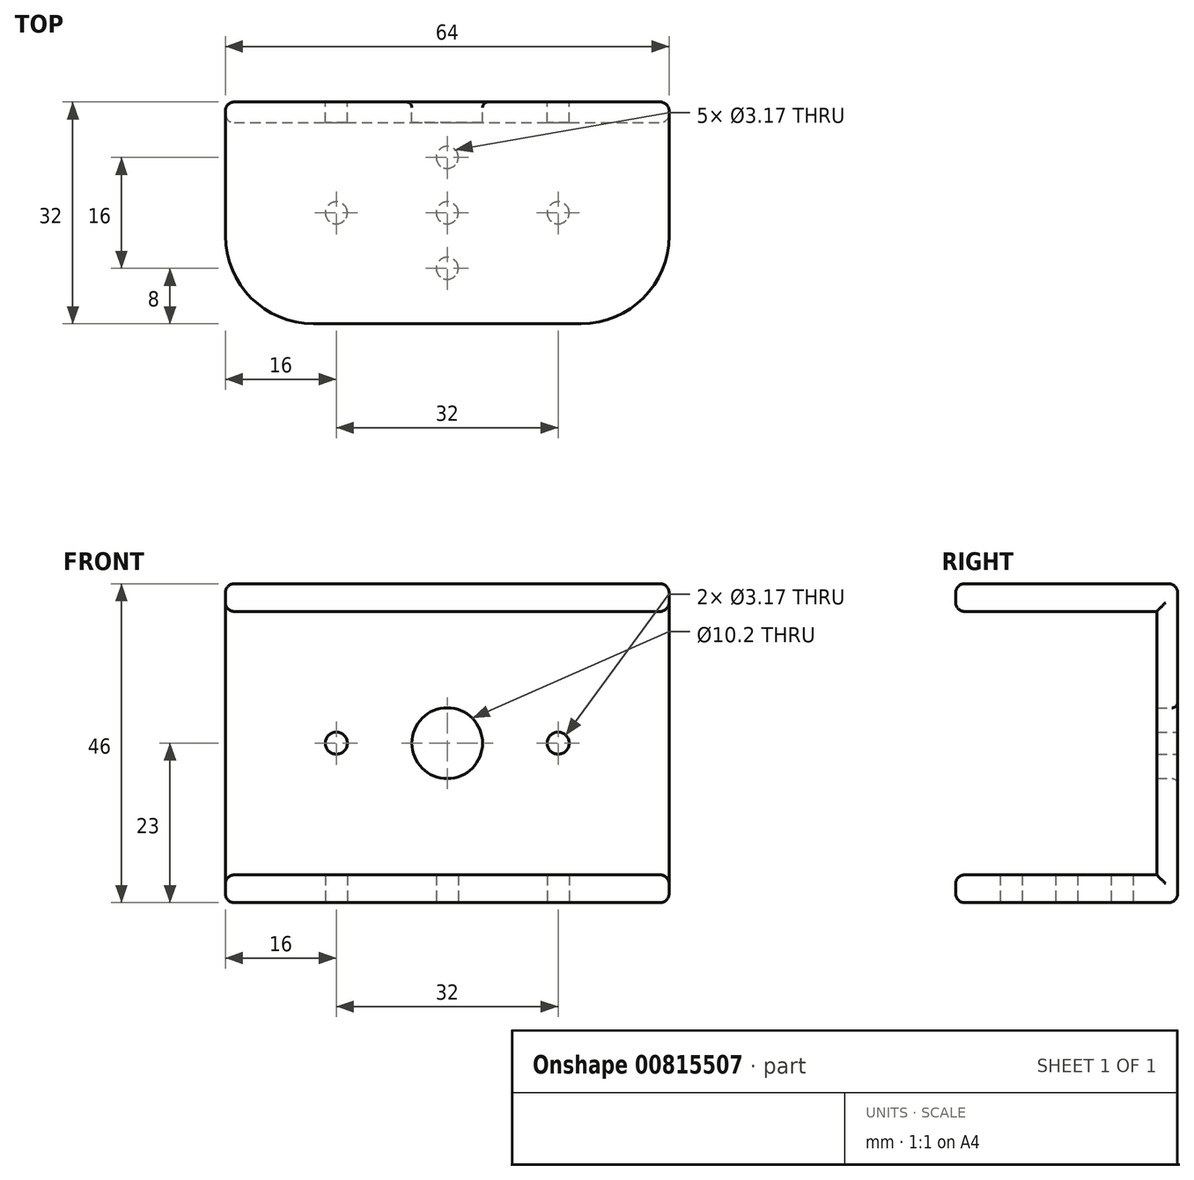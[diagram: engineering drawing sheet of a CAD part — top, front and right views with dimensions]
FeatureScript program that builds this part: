
annotation { "Feature Type Name" : "Feature", "Feature Type Description" : "" }
export const myFeature = defineFeature(function(context is Context, id is Id, definition is map)
    precondition{}
    {
        {
            var Q0;
            Q0=qCreatedBy(makeId("Front.planeOp"),FACE);
            var sketch = newSketch(context, id + "F0", { "sketchPlane" : qUnion([Q0])});
            skLineSegment(sketch, "E0", {"start": v(64, 0) * mm, "end": v(64, 38) * mm});
            skLineSegment(sketch, "E1", {"start": v(64, 38) * mm, "end": v(0, 38) * mm});
            skLineSegment(sketch, "E2", {"start": v(0, 38) * mm, "end": v(0, 0) * mm});
            skLineSegment(sketch, "E3", {"start": v(0, 0) * mm, "end": v(64, 0) * mm});
            skLineSegment(sketch, "E4", {"start": v(0, 19) * mm, "end": v(64, 19) * mm, "construction": true});
            skLineSegment(sketch, "E5", {"start": v(32, 38) * mm, "end": v(32, 0) * mm, "construction": true});
            skCircle(sketch, "E6", {"center": v(32, 19) * mm, "radius": 5.1 * mm});
            skLineSegment(sketch, "E7", {"start": v(0, 19) * mm, "end": v(32, 19) * mm, "construction": true});
            skLineSegment(sketch, "E8", {"start": v(32, 19) * mm, "end": v(64, 19) * mm, "construction": true});
            skCircle(sketch, "E9", {"center": v(16, 19) * mm, "radius": 1.59 * mm});
            skCircle(sketch, "E10", {"center": v(48, 19) * mm, "radius": 1.59 * mm});
            skLineSegment(sketch, "E11", {"start": v(0, 38) * mm, "end": v(0, 42) * mm});
            skLineSegment(sketch, "E12", {"start": v(0, 42) * mm, "end": v(64, 42) * mm});
            skLineSegment(sketch, "E13", {"start": v(64, 42) * mm, "end": v(64, 38) * mm});
            skLineSegment(sketch, "E14", {"start": v(64, 0) * mm, "end": v(64, -4) * mm});
            skLineSegment(sketch, "E15", {"start": v(64, -4) * mm, "end": v(0, -4) * mm});
            skLineSegment(sketch, "E16", {"start": v(0, -4) * mm, "end": v(0, 0) * mm});
            skSolve(sketch);
        }
        {
            var Q0;
            Q0=makeQuery(id+"F0.imprint","IMPRINT",FACE,{"disambiguationData":[TD([[makeQuery(id+"F0.imprint","IMPRINT",EDGE,{"derivedFrom":sQuery(id+"F0.wireOp",EDGE,"E0")}),1.0]])]});
            extrude(context, id + "F1", {"entities" : qUnion([Q0]), "depth" : 3 * mm, "offsetDistance" : 25.4 * mm});
        }
        {
            var Q0;
            Q0=makeQuery(id+"F0.imprint","IMPRINT",FACE,{"disambiguationData":[TD([[makeQuery(id+"F0.imprint","IMPRINT",EDGE,{"derivedFrom":sQuery(id+"F0.wireOp",EDGE,"E1")}),-1.0]])]});
            var Q1;
            Q1=makeQuery(id+"F0.imprint","IMPRINT",FACE,{"disambiguationData":[TD([[makeQuery(id+"F0.imprint","IMPRINT",EDGE,{"derivedFrom":sQuery(id+"F0.wireOp",EDGE,"E3")}),-1.0]])]});
            extrude(context, id + "F2", {"entities" : qUnion([Q0, Q1]), "operationType" : NewBodyOperationType.ADD, "depth" : 32 * mm, "offsetDistance" : 25.4 * mm});
        }
        {
            var Q0;
            Q0=makeQuery(id+"F2.opExtrude","CAP_EDGE",EDGE,{"disambiguationData":[OSD([sQuery(id+"F0.wireOp",EDGE,"E14")])],"isStart":false});
            var Q1;
            Q1=makeQuery(id+"F2.opExtrude","CAP_EDGE",EDGE,{"disambiguationData":[OSD([sQuery(id+"F0.wireOp",EDGE,"E13")])],"isStart":false});
            var Q2;
            Q2=makeQuery(id+"F2.opExtrude","CAP_EDGE",EDGE,{"disambiguationData":[OSD([sQuery(id+"F0.wireOp",EDGE,"E16")])],"isStart":false});
            var Q3;
            Q3=makeQuery(id+"F2.opExtrude","CAP_EDGE",EDGE,{"disambiguationData":[OSD([sQuery(id+"F0.wireOp",EDGE,"E11")])],"isStart":false});
            fillet(context, id + "F3", {"entities" : qUnion([Q0, Q1, Q2, Q3]), "radius" : 12.7 * mm, "tangentPropagation" : true, "allowEdgeOverflow" : false});
        }
        {
            var Q0;
            Q0=makeQuery(id+"F2.opExtrude","SWEPT_FACE",FACE,{"disambiguationData":[OSD([sQuery(id+"F0.wireOp",EDGE,"E15")])]});
            var sketch = newSketch(context, id + "F4", { "sketchPlane" : qUnion([Q0])});
            skLineSegment(sketch, "E17", {"start": v(32, 32) * mm, "end": v(32, 0) * mm, "construction": true});
            skLineSegment(sketch, "E18", {"start": v(32, 16) * mm, "end": v(64, 16) * mm, "construction": true});
            skLineSegment(sketch, "E19", {"start": v(32, 16) * mm, "end": v(0, 16) * mm, "construction": true});
            skCircle(sketch, "E20", {"center": v(16, 16) * mm, "radius": 1.59 * mm});
            skCircle(sketch, "E21", {"center": v(32, 16) * mm, "radius": 1.59 * mm});
            skCircle(sketch, "E22", {"center": v(48, 16) * mm, "radius": 1.59 * mm});
            skLineSegment(sketch, "E23", {"start": v(32, 16) * mm, "end": v(32, 32) * mm, "construction": true});
            skLineSegment(sketch, "E24", {"start": v(32, 16) * mm, "end": v(32, 0) * mm, "construction": true});
            skCircle(sketch, "E25", {"center": v(32, 8) * mm, "radius": 1.59 * mm});
            skCircle(sketch, "E26", {"center": v(32, 24) * mm, "radius": 1.59 * mm});
            skSolve(sketch);
        }
        {
            var Q0;
            Q0=makeQuery(id+"F4.imprint","IMPRINT",FACE,{"disambiguationData":[TD([[makeQuery(id+"F4.imprint","IMPRINT",EDGE,{"derivedFrom":sQuery(id+"F4.wireOp",EDGE,"E22")}),1.0]])]});
            var Q1;
            Q1=makeQuery(id+"F4.imprint","IMPRINT",FACE,{"disambiguationData":[TD([[makeQuery(id+"F4.imprint","IMPRINT",EDGE,{"derivedFrom":sQuery(id+"F4.wireOp",EDGE,"E26")}),1.0]])]});
            var Q2;
            Q2=makeQuery(id+"F4.imprint","IMPRINT",FACE,{"disambiguationData":[TD([[makeQuery(id+"F4.imprint","IMPRINT",EDGE,{"derivedFrom":sQuery(id+"F4.wireOp",EDGE,"E21")}),1.0]])]});
            var Q3;
            Q3=makeQuery(id+"F4.imprint","IMPRINT",FACE,{"disambiguationData":[TD([[makeQuery(id+"F4.imprint","IMPRINT",EDGE,{"derivedFrom":sQuery(id+"F4.wireOp",EDGE,"E25")}),1.0]])]});
            var Q4;
            Q4=makeQuery(id+"F4.imprint","IMPRINT",FACE,{"disambiguationData":[TD([[makeQuery(id+"F4.imprint","IMPRINT",EDGE,{"derivedFrom":sQuery(id+"F4.wireOp",EDGE,"E20")}),1.0]])]});
            var Q5;
            Q5=sQuery(id+"F4.wireOp",EDGE,"E20");
            var Q6;
            Q6=sQuery(id+"F4.wireOp",EDGE,"E25");
            var Q7;
            Q7=sQuery(id+"F4.wireOp",EDGE,"E21");
            var Q8;
            Q8=sQuery(id+"F4.wireOp",EDGE,"E26");
            var Q9;
            Q9=sQuery(id+"F4.wireOp",EDGE,"E22");
            var Q10;
            Q10=makeQuery(id+"F2.opExtrude","SWEPT_FACE",FACE,{"disambiguationData":[OSD([sQuery(id+"F0.wireOp",EDGE,"E3")])]});
            extrude(context, id + "F5", {"entities" : qUnion([Q0, Q1, Q2, Q3, Q4]), "operationType" : NewBodyOperationType.REMOVE, "surfaceEntities" : qUnion([Q5, Q6, Q7, Q8, Q9]), "endBound" : BoundingType.UP_TO_SURFACE, "oppositeDirection" : true, "depth" : 25.4 * mm, "endBoundEntityFace" : qUnion([Q10]), "offsetDistance" : 25.4 * mm});
        }
        {
            var Q0;
            Q0=makeQuery(id+"F2.opExtrude","SWEPT_EDGE",EDGE,{"disambiguationData":[OSD([sQuery(id+"F0.wireOp",EDGE,"E1"),sQuery(id+"F0.wireOp",EDGE,"E2"),sQuery(id+"F0.wireOp",EDGE,"E11")])]});
            var Q1;
            Q1=makeQuery(id+"F2.opExtrude","SWEPT_EDGE",EDGE,{"disambiguationData":[OSD([sQuery(id+"F0.wireOp",EDGE,"E11"),sQuery(id+"F0.wireOp",EDGE,"E12")])]});
            var Q2;
            Q2=makeQuery(id+"F2.opExtrude","SWEPT_EDGE",EDGE,{"disambiguationData":[OSD([sQuery(id+"F0.wireOp",EDGE,"E15"),sQuery(id+"F0.wireOp",EDGE,"E16")])]});
            var Q3;
            Q3=makeQuery(id+"F2.opExtrude","SWEPT_EDGE",EDGE,{"disambiguationData":[OSD([sQuery(id+"F0.wireOp",EDGE,"E2"),sQuery(id+"F0.wireOp",EDGE,"E3"),sQuery(id+"F0.wireOp",EDGE,"E16")])]});
            var Q4;
            Q4=makeQuery(id+"F1.opExtrude","CAP_EDGE",EDGE,{"disambiguationData":[OSD([sQuery(id+"F0.wireOp",EDGE,"E2")])],"isStart":false});
            var Q5;
            Q5=makeQuery(id+"F1.opExtrude","CAP_EDGE",EDGE,{"disambiguationData":[OSD([sQuery(id+"F0.wireOp",EDGE,"E0")])],"isStart":false});
            fillet(context, id + "F6", {"entities" : qUnion([Q0, Q1, Q2, Q3, Q4, Q5]), "radius" : 1.27 * mm, "tangentPropagation" : true, "allowEdgeOverflow" : false});
        }
        {
            var Q0;
            Q0=makeQuery(id+"F1.opExtrude","CAP_EDGE",EDGE,{"disambiguationData":[OSD([sQuery(id+"F0.wireOp",EDGE,"E6")])],"isStart":true});
            fillet(context, id + "F7", {"entities" : qUnion([Q0]), "radius" : .8 * mm, "tangentPropagation" : true, "allowEdgeOverflow" : false});
        }
        {
            var Q0;
            Q0=makeQuery(id+"F2.opExtrude","CAP_EDGE",EDGE,{"disambiguationData":[OSD([sQuery(id+"F0.wireOp",EDGE,"E15")])],"isStart":true});
            var Q1;
            Q1=makeQuery(id+"F2.opExtrude","CAP_EDGE",EDGE,{"disambiguationData":[OSD([sQuery(id+"F0.wireOp",EDGE,"E12")])],"isStart":true});
            fillet(context, id + "F8", {"entities" : qUnion([Q0, Q1]), "radius" : 1.27 * mm, "tangentPropagation" : true, "allowEdgeOverflow" : false});
        }
    });
